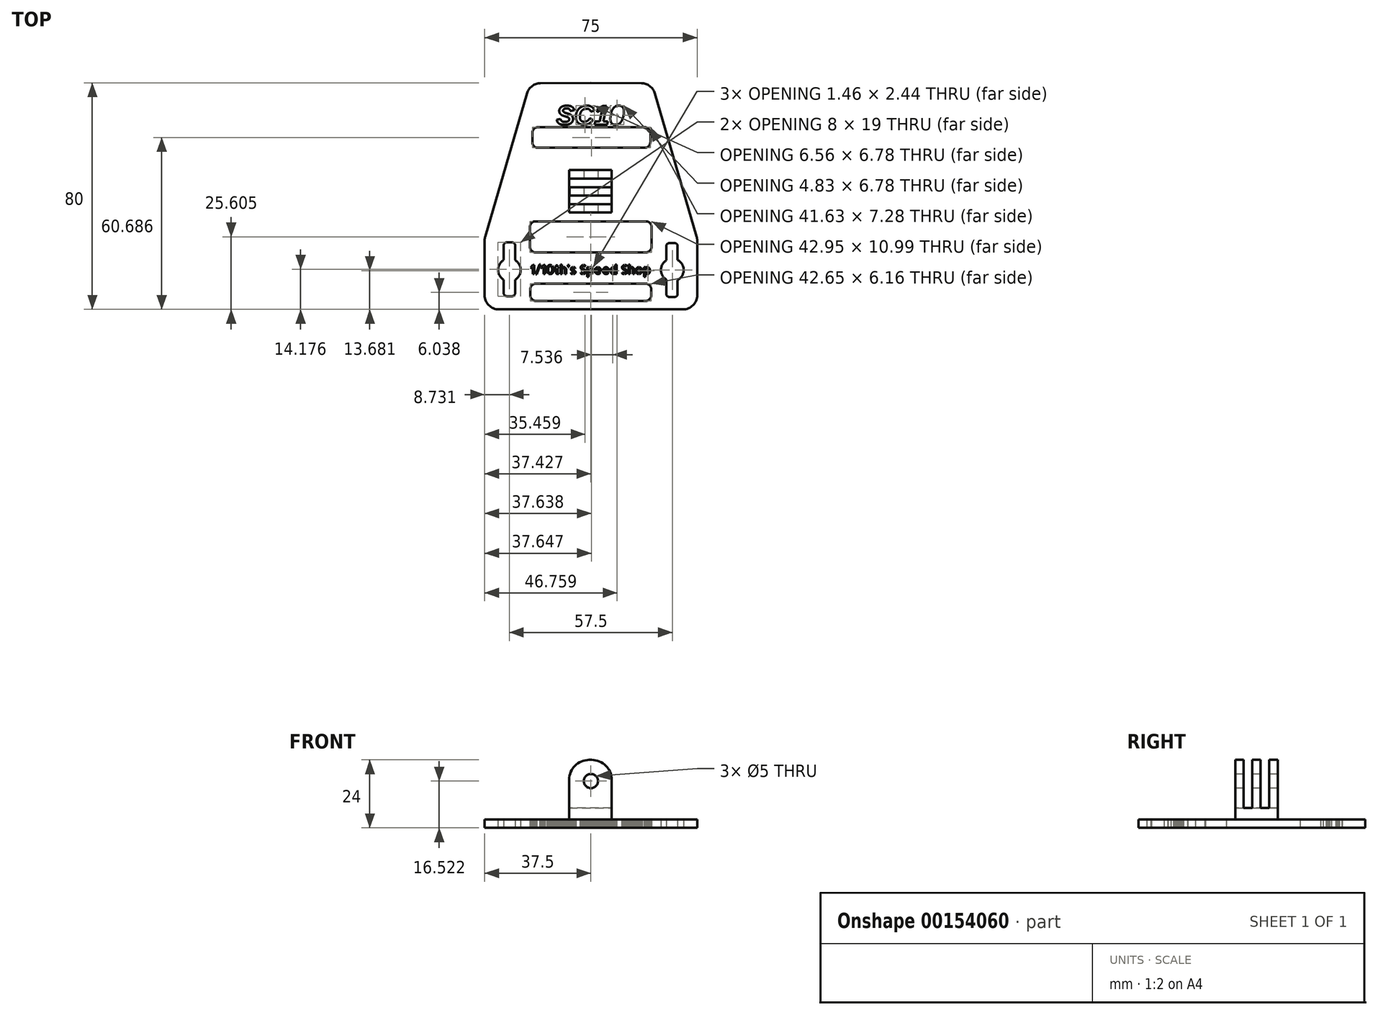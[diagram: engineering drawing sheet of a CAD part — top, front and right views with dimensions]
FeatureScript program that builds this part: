
annotation { "Feature Type Name" : "Feature", "Feature Type Description" : "" }
export const myFeature = defineFeature(function(context is Context, id is Id, definition is map)
    precondition{}
    {
        {
            var Q0;
            Q0=qCreatedBy(makeId("Top.planeOp"),FACE);
            var sketch = newSketch(context, id + "F0", { "sketchPlane" : qUnion([Q0])});
            skLineSegment(sketch, "E0", {"start": v(0, -41.39) * mm, "end": v(-32.5, -41.39) * mm});
            skLineSegment(sketch, "E1", {"start": v(-37.5, -36.39) * mm, "end": v(-37.5, -17.1) * mm});
            skLineSegment(sketch, "E2", {"start": v(-37.3, -15.7) * mm, "end": v(-22.54, 34.85) * mm});
            skLineSegment(sketch, "E3", {"start": v(-17.79, 38.45) * mm, "end": v(0, 38.61) * mm});
            skLineSegment(sketch, "E4.MirrorCS", {"start": v(17.79, 38.45) * mm, "end": v(0, 38.61) * mm});
            skLineSegment(sketch, "E5.MirrorCS", {"start": v(37.3, -15.7) * mm, "end": v(22.54, 34.85) * mm});
            skLineSegment(sketch, "E6.MirrorCS", {"start": v(37.5, -36.39) * mm, "end": v(37.5, -17.1) * mm});
            skLineSegment(sketch, "E7.MirrorCS", {"start": v(0, -41.39) * mm, "end": v(32.5, -41.39) * mm});
            skPoint(sketch, "E8.visualSharp", {"position": v(-37.5, -41.39) * mm});
            skArc(sketch, "E8.filletArc", {"start": v(-37.5, -36.39) * mm, "mid": v(-36.04, -39.93) * mm, "end": v(-32.5, -41.39) * mm});
            skPoint(sketch, "E9.visualSharp", {"position": v(37.5, -41.39) * mm});
            skArc(sketch, "E9.filletArc", {"start": v(32.5, -41.39) * mm, "mid": v(36.04, -39.93) * mm, "end": v(37.5, -36.39) * mm});
            skPoint(sketch, "E10.visualSharp", {"position": v(21.5, 38.41) * mm});
            skArc(sketch, "E10.filletArc", {"start": v(22.54, 34.85) * mm, "mid": v(20.76, 37.43) * mm, "end": v(17.79, 38.45) * mm});
            skPoint(sketch, "E11.visualSharp", {"position": v(-21.5, 38.41) * mm});
            skArc(sketch, "E11.filletArc", {"start": v(-17.79, 38.45) * mm, "mid": v(-20.76, 37.43) * mm, "end": v(-22.54, 34.85) * mm});
            skPoint(sketch, "E12.visualSharp", {"position": v(37.5, -16.38) * mm});
            skArc(sketch, "E12.filletArc", {"start": v(37.5, -17.1) * mm, "mid": v(37.45, -16.38) * mm, "end": v(37.3, -15.7) * mm});
            skPoint(sketch, "E13.visualSharp", {"position": v(-37.5, -16.38) * mm});
            skArc(sketch, "E13.filletArc", {"start": v(-37.3, -15.7) * mm, "mid": v(-37.45, -16.38) * mm, "end": v(-37.5, -17.1) * mm});
            skCircle(sketch, "E14", {"center": v(-28.77, -27.45) * mm, "radius": 4 * mm});
            skLineSegment(sketch, "E15.bottom", {"start": v(-29.73, -17.71) * mm, "end": v(-27.78, -17.71) * mm});
            skLineSegment(sketch, "E15.top", {"start": v(-29.73, -36.71) * mm, "end": v(-27.78, -36.71) * mm});
            skLineSegment(sketch, "E15.left", {"start": v(-30.76, -18.74) * mm, "end": v(-30.76, -35.7) * mm});
            skLineSegment(sketch, "E15.right", {"start": v(-26.76, -18.74) * mm, "end": v(-26.76, -35.7) * mm});
            skPoint(sketch, "E16.visualSharp", {"position": v(-30.76, -17.71) * mm});
            skArc(sketch, "E16.filletArc", {"start": v(-29.73, -17.71) * mm, "mid": v(-30.46, -18.01) * mm, "end": v(-30.76, -18.74) * mm});
            skPoint(sketch, "E17.visualSharp", {"position": v(-26.76, -36.71) * mm});
            skArc(sketch, "E17.filletArc", {"start": v(-27.78, -36.71) * mm, "mid": v(-27.05, -36.41) * mm, "end": v(-26.76, -35.7) * mm});
            skPoint(sketch, "E18.visualSharp", {"position": v(-30.76, -36.71) * mm});
            skArc(sketch, "E18.filletArc", {"start": v(-30.76, -35.7) * mm, "mid": v(-30.46, -36.41) * mm, "end": v(-29.73, -36.71) * mm});
            skPoint(sketch, "E19.visualSharp", {"position": v(-26.76, -17.71) * mm});
            skArc(sketch, "E19.filletArc", {"start": v(-26.76, -18.74) * mm, "mid": v(-27.05, -18.01) * mm, "end": v(-27.78, -17.71) * mm});
            skCircle(sketch, "E20", {"center": v(28.73, -27.49) * mm, "radius": 4 * mm});
            skLineSegment(sketch, "E21.bottom", {"start": v(27.63, -18) * mm, "end": v(29.58, -18) * mm});
            skLineSegment(sketch, "E21.top", {"start": v(27.63, -37) * mm, "end": v(29.58, -37) * mm});
            skLineSegment(sketch, "E21.left", {"start": v(26.6, -19.02) * mm, "end": v(26.6, -35.98) * mm});
            skLineSegment(sketch, "E21.right", {"start": v(30.6, -19.02) * mm, "end": v(30.6, -35.98) * mm});
            skPoint(sketch, "E22.visualSharp", {"position": v(26.6, -18) * mm});
            skArc(sketch, "E22.filletArc", {"start": v(27.63, -18) * mm, "mid": v(26.9, -18.3) * mm, "end": v(26.6, -19.02) * mm});
            skPoint(sketch, "E23.visualSharp", {"position": v(30.6, -37) * mm});
            skArc(sketch, "E23.filletArc", {"start": v(29.58, -37) * mm, "mid": v(30.3, -36.7) * mm, "end": v(30.6, -35.98) * mm});
            skPoint(sketch, "E24.visualSharp", {"position": v(26.6, -37) * mm});
            skArc(sketch, "E24.filletArc", {"start": v(26.6, -35.98) * mm, "mid": v(26.9, -36.7) * mm, "end": v(27.63, -37) * mm});
            skPoint(sketch, "E25.visualSharp", {"position": v(30.6, -18) * mm});
            skArc(sketch, "E25.filletArc", {"start": v(30.6, -19.02) * mm, "mid": v(30.3, -18.3) * mm, "end": v(29.58, -18) * mm});
            skText(sketch, "E26", { "text": "1/10th\'s Speed Shop", "fontName": "AllertaStencil-Regular.ttf"});
            skText(sketch, "E27", { "text": "SC10", "fontName": "Arimo-BoldItalic.ttf"});
            skLineSegment(sketch, "E28.bottom", {"start": v(-19.55, -10.29) * mm, "end": v(19.4, -10.29) * mm});
            skLineSegment(sketch, "E28.top", {"start": v(-19.55, -21.28) * mm, "end": v(19.4, -21.28) * mm});
            skLineSegment(sketch, "E28.left", {"start": v(-21.55, -12.29) * mm, "end": v(-21.55, -19.28) * mm});
            skLineSegment(sketch, "E28.right", {"start": v(21.4, -12.29) * mm, "end": v(21.4, -19.28) * mm});
            skLineSegment(sketch, "E29.bottom", {"start": v(-19.4, -32.27) * mm, "end": v(19.25, -32.27) * mm});
            skLineSegment(sketch, "E29.top", {"start": v(-19.4, -38.43) * mm, "end": v(19.25, -38.43) * mm});
            skLineSegment(sketch, "E29.left", {"start": v(-21.4, -34.27) * mm, "end": v(-21.4, -36.43) * mm});
            skLineSegment(sketch, "E29.right", {"start": v(21.25, -34.27) * mm, "end": v(21.25, -36.43) * mm});
            skLineSegment(sketch, "E30.bottom", {"start": v(-18.67, 22.94) * mm, "end": v(18.96, 22.94) * mm});
            skLineSegment(sketch, "E30.top", {"start": v(-18.67, 15.66) * mm, "end": v(18.96, 15.66) * mm});
            skLineSegment(sketch, "E30.left", {"start": v(-20.67, 20.94) * mm, "end": v(-20.67, 17.66) * mm});
            skLineSegment(sketch, "E30.right", {"start": v(20.96, 20.94) * mm, "end": v(20.96, 17.66) * mm});
            skPoint(sketch, "E31.visualSharp", {"position": v(-20.67, 22.94) * mm});
            skArc(sketch, "E31.filletArc", {"start": v(-18.67, 22.94) * mm, "mid": v(-20.08, 22.35) * mm, "end": v(-20.67, 20.94) * mm});
            skPoint(sketch, "E32.visualSharp", {"position": v(-20.67, 15.66) * mm});
            skArc(sketch, "E32.filletArc", {"start": v(-20.67, 17.66) * mm, "mid": v(-20.08, 16.24) * mm, "end": v(-18.67, 15.66) * mm});
            skPoint(sketch, "E33.visualSharp", {"position": v(20.96, 22.94) * mm});
            skArc(sketch, "E33.filletArc", {"start": v(20.96, 20.94) * mm, "mid": v(20.37, 22.35) * mm, "end": v(18.96, 22.94) * mm});
            skPoint(sketch, "E34.visualSharp", {"position": v(20.96, 15.66) * mm});
            skArc(sketch, "E34.filletArc", {"start": v(18.96, 15.66) * mm, "mid": v(20.37, 16.24) * mm, "end": v(20.96, 17.66) * mm});
            skPoint(sketch, "E35.visualSharp", {"position": v(-21.55, -10.29) * mm});
            skArc(sketch, "E35.filletArc", {"start": v(-19.55, -10.29) * mm, "mid": v(-20.96, -10.87) * mm, "end": v(-21.55, -12.29) * mm});
            skPoint(sketch, "E36.visualSharp", {"position": v(21.4, -10.29) * mm});
            skArc(sketch, "E36.filletArc", {"start": v(21.4, -12.29) * mm, "mid": v(20.81, -10.87) * mm, "end": v(19.4, -10.29) * mm});
            skPoint(sketch, "E37.visualSharp", {"position": v(21.4, -21.28) * mm});
            skArc(sketch, "E37.filletArc", {"start": v(19.4, -21.28) * mm, "mid": v(20.81, -20.7) * mm, "end": v(21.4, -19.28) * mm});
            skPoint(sketch, "E38.visualSharp", {"position": v(-21.55, -21.28) * mm});
            skArc(sketch, "E38.filletArc", {"start": v(-21.55, -19.28) * mm, "mid": v(-20.96, -20.7) * mm, "end": v(-19.55, -21.28) * mm});
            skPoint(sketch, "E39.visualSharp", {"position": v(-21.4, -32.27) * mm});
            skArc(sketch, "E39.filletArc", {"start": v(-19.4, -32.27) * mm, "mid": v(-20.81, -32.86) * mm, "end": v(-21.4, -34.27) * mm});
            skPoint(sketch, "E40.visualSharp", {"position": v(-21.4, -38.43) * mm});
            skArc(sketch, "E40.filletArc", {"start": v(-21.4, -36.43) * mm, "mid": v(-20.81, -37.84) * mm, "end": v(-19.4, -38.43) * mm});
            skPoint(sketch, "E41.visualSharp", {"position": v(21.25, -32.27) * mm});
            skArc(sketch, "E41.filletArc", {"start": v(21.25, -34.27) * mm, "mid": v(20.67, -32.86) * mm, "end": v(19.25, -32.27) * mm});
            skPoint(sketch, "E42.visualSharp", {"position": v(21.25, -38.43) * mm});
            skArc(sketch, "E42.filletArc", {"start": v(19.25, -38.43) * mm, "mid": v(20.67, -37.84) * mm, "end": v(21.25, -36.43) * mm});
            const initialGuessF0  = {"E26": [-0.02141, -0.02891, 1, 0, 0.00314], "E27": [-0.01217, 0.02386, 1, 0, 0.00689]};
            skSetInitialGuess(sketch, initialGuessF0);
            skSolve(sketch);
        }
        {
            var Q0;
            Q0=makeQuery(id+"F0.imprint","IMPRINT",FACE,{"disambiguationData":[TD([[makeQuery(id+"F0.imprint","IMPRINT",EDGE,{"derivedFrom":sQuery(id+"F0.wireOp",EDGE,"E0")}),-1.0]])]});
            extrude(context, id + "F1", {"entities" : qUnion([Q0]), "depth" : 3 * mm});
        }
        {
            var Q0;
            Q0=makeQuery(id+"F1.opExtrude","CAP_FACE",FACE,{"disambiguationData":[OSD([sQuery(id+"F0.wireOp",EDGE,"E0"),sQuery(id+"F0.wireOp",EDGE,"E1"),sQuery(id+"F0.wireOp",EDGE,"E2"),sQuery(id+"F0.wireOp",EDGE,"E3"),sQuery(id+"F0.wireOp",EDGE,"E4.MirrorCS"),sQuery(id+"F0.wireOp",EDGE,"E5.MirrorCS"),sQuery(id+"F0.wireOp",EDGE,"E6.MirrorCS"),sQuery(id+"F0.wireOp",EDGE,"E7.MirrorCS"),sQuery(id+"F0.wireOp",EDGE,"E8.filletArc"),sQuery(id+"F0.wireOp",EDGE,"E9.filletArc"),sQuery(id+"F0.wireOp",EDGE,"E10.filletArc"),sQuery(id+"F0.wireOp",EDGE,"E11.filletArc"),sQuery(id+"F0.wireOp",EDGE,"E12.filletArc"),sQuery(id+"F0.wireOp",EDGE,"E13.filletArc"),sQuery(id+"F0.wireOp",EDGE,"E14"),sQuery(id+"F0.wireOp",EDGE,"E15.bottom"),sQuery(id+"F0.wireOp",EDGE,"E15.top"),sQuery(id+"F0.wireOp",EDGE,"E15.left"),sQuery(id+"F0.wireOp",EDGE,"E15.right"),sQuery(id+"F0.wireOp",EDGE,"E16.filletArc"),sQuery(id+"F0.wireOp",EDGE,"E17.filletArc"),sQuery(id+"F0.wireOp",EDGE,"E18.filletArc"),sQuery(id+"F0.wireOp",EDGE,"E19.filletArc"),sQuery(id+"F0.wireOp",EDGE,"E20"),sQuery(id+"F0.wireOp",EDGE,"E21.bottom"),sQuery(id+"F0.wireOp",EDGE,"E21.top"),sQuery(id+"F0.wireOp",EDGE,"E21.left"),sQuery(id+"F0.wireOp",EDGE,"E21.right"),sQuery(id+"F0.wireOp",EDGE,"E22.filletArc"),sQuery(id+"F0.wireOp",EDGE,"E23.filletArc"),sQuery(id+"F0.wireOp",EDGE,"E24.filletArc"),sQuery(id+"F0.wireOp",EDGE,"E25.filletArc")])],"isStart":false});
            var sketch = newSketch(context, id + "F2", { "sketchPlane" : qUnion([Q0])});
            skLineSegment(sketch, "E43.bottom", {"start": v(-7.7, 7.82) * mm, "end": v(7.3, 7.82) * mm});
            skLineSegment(sketch, "E43.top", {"start": v(-7.7, -7.18) * mm, "end": v(7.3, -7.18) * mm});
            skLineSegment(sketch, "E43.left", {"start": v(-7.7, 7.82) * mm, "end": v(-7.7, -7.18) * mm});
            skLineSegment(sketch, "E43.right", {"start": v(7.3, 7.82) * mm, "end": v(7.3, -7.18) * mm});
            skSolve(sketch);
        }
        {
            var Q0;
            Q0=makeQuery(id+"F2.imprint","IMPRINT",FACE,{"disambiguationData":[TD([[makeQuery(id+"F2.imprint","IMPRINT",EDGE,{"derivedFrom":sQuery(id+"F2.wireOp",EDGE,"E43.bottom")}),-1.0]])]});
            extrude(context, id + "F3", {"entities" : qUnion([Q0]), "operationType" : NewBodyOperationType.ADD, "depth" : 4 * mm});
        }
        {
            var Q0;
            Q0=makeQuery(id+"F3.opExtrude","CAP_FACE",FACE,{"disambiguationData":[OSD([sQuery(id+"F2.wireOp",EDGE,"E43.bottom"),sQuery(id+"F2.wireOp",EDGE,"E43.top"),sQuery(id+"F2.wireOp",EDGE,"E43.left"),sQuery(id+"F2.wireOp",EDGE,"E43.right")])],"isStart":false});
            var sketch = newSketch(context, id + "F4", { "sketchPlane" : qUnion([Q0])});
            skLineSegment(sketch, "E44.bottom", {"start": v(7.33, 4.78) * mm, "end": v(-7.67, 4.78) * mm});
            skLineSegment(sketch, "E44.top", {"start": v(7.33, 7.78) * mm, "end": v(-7.67, 7.78) * mm});
            skLineSegment(sketch, "E44.left", {"start": v(7.33, 4.78) * mm, "end": v(7.33, 7.78) * mm});
            skLineSegment(sketch, "E44.right", {"start": v(-7.67, 4.78) * mm, "end": v(-7.67, 7.78) * mm});
            skPoint(sketch, "E44.middle", {"position": v(-0.17, 6.28) * mm});
            skLineSegment(sketch, "E45.bottom", {"start": v(7.42, -1.22) * mm, "end": v(-7.58, -1.22) * mm});
            skLineSegment(sketch, "E45.top", {"start": v(7.42, 1.78) * mm, "end": v(-7.58, 1.78) * mm});
            skLineSegment(sketch, "E45.left", {"start": v(7.42, -1.22) * mm, "end": v(7.42, 1.78) * mm});
            skLineSegment(sketch, "E45.right", {"start": v(-7.58, -1.22) * mm, "end": v(-7.58, 1.78) * mm});
            skPoint(sketch, "E45.middle", {"position": v(-0.08, 0.28) * mm});
            skLineSegment(sketch, "E46.bottom", {"start": v(7.33, -7.22) * mm, "end": v(-7.67, -7.22) * mm});
            skLineSegment(sketch, "E46.top", {"start": v(7.33, -4.22) * mm, "end": v(-7.67, -4.22) * mm});
            skLineSegment(sketch, "E46.left", {"start": v(7.33, -7.22) * mm, "end": v(7.33, -4.22) * mm});
            skLineSegment(sketch, "E46.right", {"start": v(-7.67, -7.22) * mm, "end": v(-7.67, -4.22) * mm});
            skPoint(sketch, "E46.middle", {"position": v(-0.17, -5.72) * mm});
            skSolve(sketch);
        }
        {
            var Q0;
            {var subQ0=sQuery(id+"F4.wireOp",EDGE,"E44.right");Q0=makeQuery(id+"F4.imprint","IMPRINT",FACE,{"disambiguationData":[TD([[makeQuery(id+"F4.imprint","IMPRINT",EDGE,{"derivedFrom":subQ0}),-1.0]])]});}
            var Q1;
            {var subQ0=sQuery(id+"F4.wireOp",EDGE,"E45.right");Q1=makeQuery(id+"F4.imprint","IMPRINT",FACE,{"disambiguationData":[TD([[makeQuery(id+"F4.imprint","IMPRINT",EDGE,{"derivedFrom":subQ0}),-1.0]])]});}
            var Q2;
            {var subQ0=sQuery(id+"F4.wireOp",EDGE,"E46.right");var subQ1=sQuery(id+"F4.wireOp",EDGE,"E46.top");var subQ2=makeQuery(id+"F4.imprint","INTERSECT",VERTEX,{"derivedFrom":[subQ1,subQ0]});Q2=makeQuery(id+"F4.imprint","IMPRINT",FACE,{"disambiguationData":[TD([[makeQuery(id+"F4.imprint","IMPRINT",EDGE,{"disambiguationData":[TD([[subQ2,1.0]])],"derivedFrom":subQ1}),1.0]])]});}
            extrude(context, id + "F5", {"entities" : qUnion([Q0, Q1, Q2]), "operationType" : NewBodyOperationType.ADD, "depth" : 17 * mm});
        }
        {
            var Q0;
            Q0=makeQuery(id+"F5.opExtrude","CAP_EDGE",EDGE,{"disambiguationData":[OSD([sQuery(id+"F4.wireOp",EDGE,"E44.right")])],"isStart":false});
            var Q1;
            Q1=makeQuery(id+"F5.opExtrude","CAP_EDGE",EDGE,{"disambiguationData":[OSD([sQuery(id+"F4.wireOp",EDGE,"E45.right")])],"isStart":false});
            var Q2;
            Q2=makeQuery(id+"F5.opExtrude","CAP_EDGE",EDGE,{"disambiguationData":[OSD([sQuery(id+"F4.wireOp",EDGE,"E46.right")])],"isStart":false});
            var Q3;
            {var subQ0=sQuery(id+"F2.wireOp",EDGE,"E43.right");var subQ1=makeQuery(id+"F3.opExtrude","CAP_EDGE",EDGE,{"disambiguationData":[OSD([subQ0])],"isStart":false});Q3=makeQuery(id+"F5.opExtrude","CAP_EDGE",EDGE,{"disambiguationData":[OSD([subQ0]),TDD([makeQuery(id+"F4.imprint","IMPRINT",EDGE,{"disambiguationData":[TD([[makeQuery(id+"F4.imprint","INTERSECT",VERTEX,{"derivedFrom":[makeQuery(id+"F3.opExtrude","CAP_EDGE",EDGE,{"disambiguationData":[OSD([sQuery(id+"F2.wireOp",EDGE,"E43.top")])],"isStart":false}),subQ1]}),1.0]])],"derivedFrom":subQ1})])],"isStart":false});}
            var Q4;
            {var subQ0=sQuery(id+"F2.wireOp",EDGE,"E43.right");var subQ1=makeQuery(id+"F3.opExtrude","CAP_EDGE",EDGE,{"disambiguationData":[OSD([subQ0])],"isStart":false});Q4=makeQuery(id+"F5.opExtrude","CAP_EDGE",EDGE,{"disambiguationData":[OSD([subQ0]),TDD([makeQuery(id+"F4.imprint","IMPRINT",EDGE,{"disambiguationData":[TD([[makeQuery(id+"F4.imprint","INTERSECT",VERTEX,{"derivedFrom":[subQ1,sQuery(id+"F4.wireOp",EDGE,"E45.bottom")]}),1.0]])],"derivedFrom":subQ1})])],"isStart":false});}
            var Q5;
            {var subQ0=sQuery(id+"F2.wireOp",EDGE,"E43.right");var subQ1=makeQuery(id+"F3.opExtrude","CAP_EDGE",EDGE,{"disambiguationData":[OSD([subQ0])],"isStart":false});Q5=makeQuery(id+"F5.opExtrude","CAP_EDGE",EDGE,{"disambiguationData":[OSD([subQ0]),TDD([makeQuery(id+"F4.imprint","IMPRINT",EDGE,{"disambiguationData":[TD([[makeQuery(id+"F4.imprint","INTERSECT",VERTEX,{"derivedFrom":[subQ1,sQuery(id+"F4.wireOp",EDGE,"E44.bottom")]}),1.0]])],"derivedFrom":subQ1})])],"isStart":false});}
            fillet(context, id + "F6", {"entities" : qUnion([Q0, Q1, Q2, Q3, Q4, Q5]), "radius" : 7 * mm, "tangentPropagation" : true, "allowEdgeOverflow" : false});
        }
        {
            var Q0;
            {var subQ0=sQuery(id+"F2.wireOp",EDGE,"E43.top");Q0=makeQuery(id+"F5.boolean.opBoolean","MERGE",FACE,{"derivedFrom":[makeQuery(id+"F3.opExtrude","SWEPT_FACE",FACE,{"disambiguationData":[OSD([subQ0])]}),makeQuery(id+"F5.opExtrude","SWEPT_FACE",FACE,{"disambiguationData":[OSD([subQ0])]})]});}
            var sketch = newSketch(context, id + "F7", { "sketchPlane" : qUnion([Q0])});
            skPoint(sketch, "E47", {"position": v(0, 16.52) * mm});
            skSolve(sketch);
        }
        {
            var Q0;
            Q0=sQuery(id+"F7.wireOp",VERTEX,"E47");
            var Q1;
            Q1=makeQuery(id+"F1.opExtrude","SWEPT_BODY",BODY,{"disambiguationData":[OSD([sQuery(id+"F0.wireOp",EDGE,"E0"),sQuery(id+"F0.wireOp",EDGE,"E1"),sQuery(id+"F0.wireOp",EDGE,"E2"),sQuery(id+"F0.wireOp",EDGE,"E3"),sQuery(id+"F0.wireOp",EDGE,"E4.MirrorCS"),sQuery(id+"F0.wireOp",EDGE,"E5.MirrorCS"),sQuery(id+"F0.wireOp",EDGE,"E6.MirrorCS"),sQuery(id+"F0.wireOp",EDGE,"E7.MirrorCS"),sQuery(id+"F0.wireOp",EDGE,"E8.filletArc"),sQuery(id+"F0.wireOp",EDGE,"E9.filletArc"),sQuery(id+"F0.wireOp",EDGE,"E10.filletArc"),sQuery(id+"F0.wireOp",EDGE,"E11.filletArc"),sQuery(id+"F0.wireOp",EDGE,"E12.filletArc"),sQuery(id+"F0.wireOp",EDGE,"E13.filletArc"),sQuery(id+"F0.wireOp",EDGE,"E14"),sQuery(id+"F0.wireOp",EDGE,"E15.bottom"),sQuery(id+"F0.wireOp",EDGE,"E15.top"),sQuery(id+"F0.wireOp",EDGE,"E15.left"),sQuery(id+"F0.wireOp",EDGE,"E15.right"),sQuery(id+"F0.wireOp",EDGE,"E16.filletArc"),sQuery(id+"F0.wireOp",EDGE,"E17.filletArc"),sQuery(id+"F0.wireOp",EDGE,"E18.filletArc"),sQuery(id+"F0.wireOp",EDGE,"E19.filletArc"),sQuery(id+"F0.wireOp",EDGE,"E20"),sQuery(id+"F0.wireOp",EDGE,"E21.bottom"),sQuery(id+"F0.wireOp",EDGE,"E21.top"),sQuery(id+"F0.wireOp",EDGE,"E21.left"),sQuery(id+"F0.wireOp",EDGE,"E21.right"),sQuery(id+"F0.wireOp",EDGE,"E22.filletArc"),sQuery(id+"F0.wireOp",EDGE,"E23.filletArc"),sQuery(id+"F0.wireOp",EDGE,"E24.filletArc"),sQuery(id+"F0.wireOp",EDGE,"E25.filletArc")])]});
            hole(context, id + "F8", {"style" : HoleStyle.SIMPLE, "endStyle" : HoleEndStyle.THROUGH, "holeDiameter" : 5 * mm, "locations" : qUnion([Q0]), "scope" : qUnion([Q1]), "isTappedThrough" : true});
        }
    });
